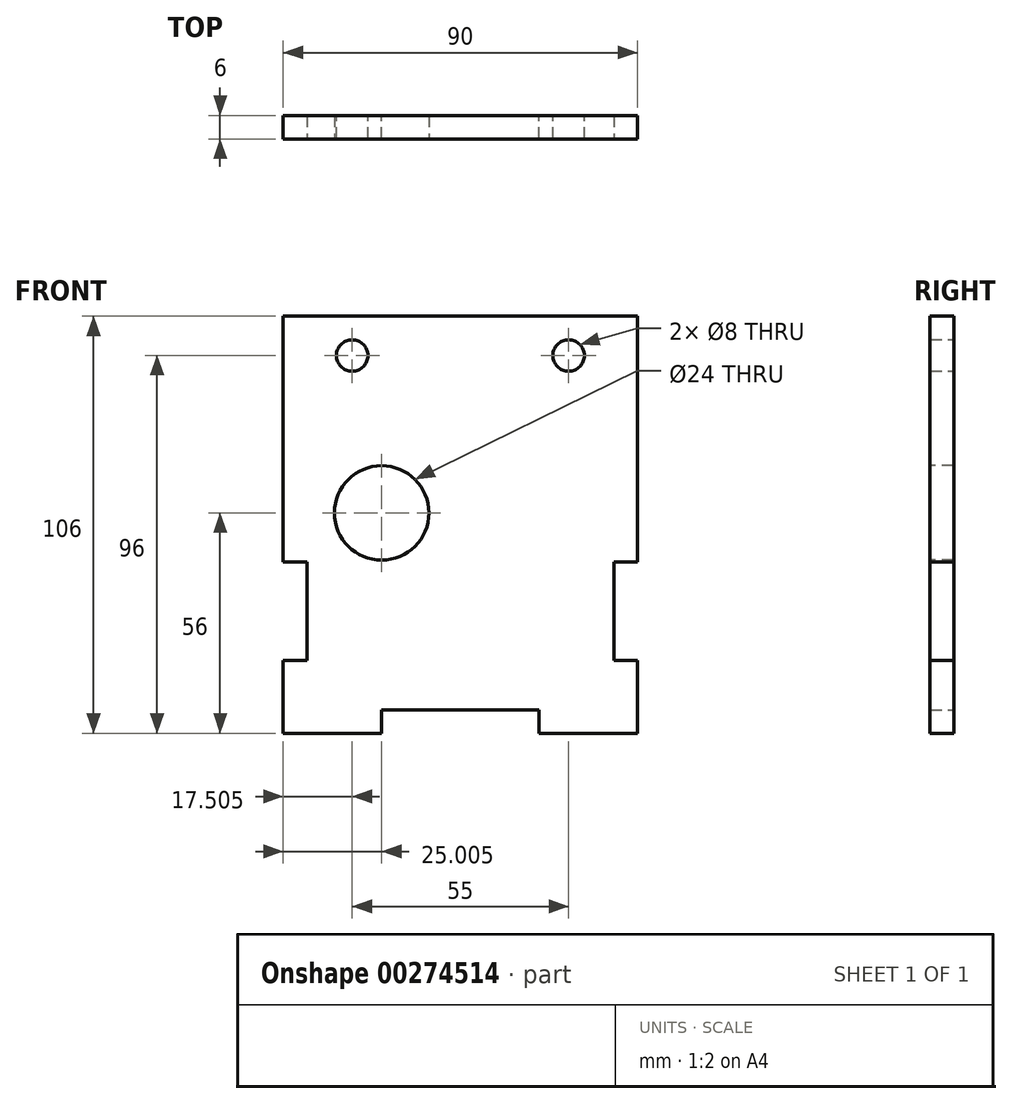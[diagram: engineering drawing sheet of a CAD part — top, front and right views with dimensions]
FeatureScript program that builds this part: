
annotation { "Feature Type Name" : "Feature", "Feature Type Description" : "" }
export const myFeature = defineFeature(function(context is Context, id is Id, definition is map)
    precondition{}
    {
        {
            var Q0;
            Q0=qCreatedBy(makeId("Front.planeOp"),FACE);
            var sketch = newSketch(context, id + "F0", { "sketchPlane" : qUnion([Q0])});
            skLineSegment(sketch, "E0.bottom", {"start": v(-32.34, 89.38) * mm, "end": v(57.66, 89.38) * mm});
            skLineSegment(sketch, "E0.top", {"start": v(-7.34, -10.62) * mm, "end": v(32.66, -10.62) * mm});
            skLineSegment(sketch, "E0.left", {"start": v(-32.34, 89.38) * mm, "end": v(-32.34, -10.62) * mm});
            skLineSegment(sketch, "E0.right", {"start": v(57.66, 89.38) * mm, "end": v(57.66, -10.62) * mm});
            skCircle(sketch, "E1", {"center": v(-14.84, 79.38) * mm, "radius": 4 * mm});
            skCircle(sketch, "E2", {"center": v(40.16, 79.38) * mm, "radius": 4 * mm});
            skLineSegment(sketch, "E3.top", {"start": v(-32.34, -16.62) * mm, "end": v(-7.34, -16.62) * mm});
            skLineSegment(sketch, "E3.left", {"start": v(-32.34, -10.62) * mm, "end": v(-32.34, -16.62) * mm});
            skLineSegment(sketch, "E3.right", {"start": v(-7.34, -10.62) * mm, "end": v(-7.34, -16.62) * mm});
            skLineSegment(sketch, "E4.top", {"start": v(57.66, -16.62) * mm, "end": v(32.66, -16.62) * mm});
            skLineSegment(sketch, "E4.left", {"start": v(57.66, -10.62) * mm, "end": v(57.66, -16.62) * mm});
            skLineSegment(sketch, "E4.right", {"start": v(32.66, -10.62) * mm, "end": v(32.66, -16.62) * mm});
            skSolve(sketch);
        }
        {
            var Q0;
            Q0 = qSketchRegion(id + "F0", true);
            extrude(context, id + "F1", {"entities" : qUnion([Q0]), "depth" : 6 * mm});
        }
        {
            var Q0;
            Q0=makeQuery(id+"F1.opExtrude","CAP_FACE",FACE,{"disambiguationData":[OSD([sQuery(id+"F0.wireOp",EDGE,"E0.bottom"),sQuery(id+"F0.wireOp",EDGE,"E0.top"),sQuery(id+"F0.wireOp",EDGE,"E0.left"),sQuery(id+"F0.wireOp",EDGE,"E0.right"),sQuery(id+"F0.wireOp",EDGE,"E1"),sQuery(id+"F0.wireOp",EDGE,"E2"),sQuery(id+"F0.wireOp",EDGE,"E3.top"),sQuery(id+"F0.wireOp",EDGE,"E3.left"),sQuery(id+"F0.wireOp",EDGE,"E3.right"),sQuery(id+"F0.wireOp",EDGE,"E4.top"),sQuery(id+"F0.wireOp",EDGE,"E4.left"),sQuery(id+"F0.wireOp",EDGE,"E4.right")])],"isStart":false});
            var sketch = newSketch(context, id + "F2", { "sketchPlane" : qUnion([Q0])});
            skCircle(sketch, "E5", {"center": v(-7.34, 39.38) * mm, "radius": 12 * mm});
            skLineSegment(sketch, "E6.bottom", {"start": v(-32.34, 26.88) * mm, "end": v(-26.34, 26.88) * mm});
            skLineSegment(sketch, "E6.top", {"start": v(-32.34, 1.88) * mm, "end": v(-26.34, 1.88) * mm});
            skLineSegment(sketch, "E6.left", {"start": v(-32.34, 26.88) * mm, "end": v(-32.34, 1.88) * mm});
            skLineSegment(sketch, "E6.right", {"start": v(-26.34, 26.88) * mm, "end": v(-26.34, 1.88) * mm});
            skLineSegment(sketch, "E7.bottom", {"start": v(51.66, 26.88) * mm, "end": v(57.66, 26.88) * mm});
            skLineSegment(sketch, "E7.top", {"start": v(51.66, 1.88) * mm, "end": v(57.66, 1.88) * mm});
            skLineSegment(sketch, "E7.left", {"start": v(51.66, 26.88) * mm, "end": v(51.66, 1.88) * mm});
            skLineSegment(sketch, "E7.right", {"start": v(57.66, 26.88) * mm, "end": v(57.66, 1.88) * mm});
            skSolve(sketch);
        }
        {
            var Q0;
            Q0 = qSketchRegion(id + "F2", true);
            extrude(context, id + "F3", {"entities" : qUnion([Q0]), "operationType" : NewBodyOperationType.REMOVE, "oppositeDirection" : true, "depth" : 25 * mm});
        }
    });
